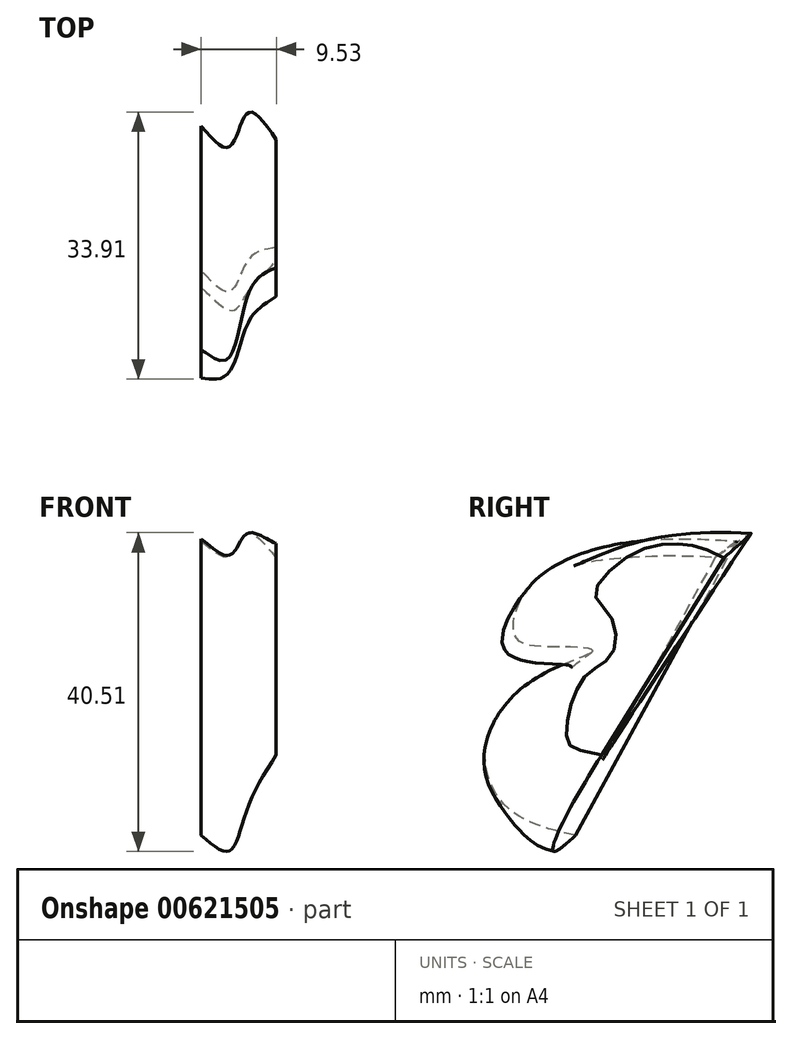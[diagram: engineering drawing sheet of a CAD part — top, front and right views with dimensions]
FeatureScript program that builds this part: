
annotation { "Feature Type Name" : "Feature", "Feature Type Description" : "" }
export const myFeature = defineFeature(function(context is Context, id is Id, definition is map)
    precondition{}
    {
        {
            var Q0;
            Q0=qCreatedBy(makeId("Right.planeOp"),FACE);
            cPlane(context, id + "F0", {"entities" : qUnion([Q0]), "cplaneType" : CPlaneType.OFFSET, "offset" : 3.17 * mm, "width" : 152.4 * mm, "height" : 152.4 * mm});
        }
        {
            var Q0;
            Q0=qCreatedBy(id+"F0.planeOp",FACE);
            cPlane(context, id + "F1", {"entities" : qUnion([Q0]), "cplaneType" : CPlaneType.OFFSET, "offset" : 3.17 * mm, "width" : 152.4 * mm, "height" : 152.4 * mm});
        }
        {
            var Q0;
            Q0=qCreatedBy(id+"F1.planeOp",FACE);
            cPlane(context, id + "F2", {"entities" : qUnion([Q0]), "cplaneType" : CPlaneType.OFFSET, "offset" : 3.17 * mm, "width" : 152.4 * mm, "height" : 152.4 * mm});
        }
        {
            var Q0;
            Q0=qCreatedBy(makeId("Right.planeOp"),FACE);
            var sketch = newSketch(context, id + "F3", { "sketchPlane" : qUnion([Q0])});
            skFitSpline(sketch, "E0", {"points": [v(0, -7.53) * mm, v(-8.5, -4.13) * mm, v(-11.42, 3.64) * mm, v(-4.62, 12.71) * mm, v(2.19, 15.95) * mm, v(-2.35, 16.44) * mm, v(-7.53, 17.57) * mm, v(-5.75, 24.21) * mm, v(6.88, 29.72) * mm, v(20.49, 29.88) * mm], "startDerivative": vector(-82.86, 19.05) * mm, "endDerivative": vector(95.34, -5.58) * mm});
            skLineSegment(sketch, "E1", {"start": v(20.49, 29.88) * mm, "end": v(0, -7.53) * mm});
            skSolve(sketch);
        }
        {
            var Q0;
            Q0=qCreatedBy(id+"F0.planeOp",FACE);
            var sketch = newSketch(context, id + "F4", { "sketchPlane" : qUnion([Q0])});
            skFitSpline(sketch, "E2", {"points": [v(-2.7, -9.56) * mm, v(-8.67, -4.62) * mm, v(-11.1, 2.83) * mm, v(-4.94, 11.1) * mm, v(-0.52, 13.92) * mm, v(-5.05, 14.4) * mm, v(-9.15, 16.6) * mm, v(-4.62, 24.54) * mm, v(5.91, 27.78) * mm, v(17.78, 27.85) * mm], "startDerivative": vector(-82.86, 19.05) * mm, "endDerivative": vector(95.34, -5.58) * mm});
            skLineSegment(sketch, "E3", {"start": v(17.78, 27.85) * mm, "end": v(-2.7, -9.56) * mm});
            skSolve(sketch);
        }
        {
            var Q0;
            Q0=qCreatedBy(id+"F1.planeOp",FACE);
            var sketch = newSketch(context, id + "F5", { "sketchPlane" : qUnion([Q0])});
            skFitSpline(sketch, "E4", {"points": [v(0, -2.83) * mm, v(-3.64, 2.67) * mm, v(-3.48, 7.53) * mm, v(0, 13.2) * mm, v(3.98, 16.89) * mm, v(1.7, 19.2) * mm, v(0, 21.14) * mm, v(3.64, 27.61) * mm, v(12.07, 30.53) * mm, v(22.28, 30.82) * mm], "startDerivative": vector(-82.86, 19.05) * mm, "endDerivative": vector(95.34, -5.58) * mm});
            skLineSegment(sketch, "E5", {"start": v(22.28, 30.82) * mm, "end": v(0, -2.83) * mm});
            skSolve(sketch);
        }
        {
            var Q0;
            Q0=qCreatedBy(id+"F2.planeOp",FACE);
            var sketch = newSketch(context, id + "F6", { "sketchPlane" : qUnion([Q0])});
            skFitSpline(sketch, "E6", {"points": [v(3.32, 2.67) * mm, v(-1, 4.42) * mm, v(-0.6, 9.07) * mm, v(1.71, 13.14) * mm, v(4.65, 15.56) * mm, v(4.46, 20.35) * mm, v(2.48, 23.18) * mm, v(7.47, 28.38) * mm, v(13.55, 29.48) * mm, v(18.82, 27.72) * mm], "startDerivative": vector(-82.86, 19.05) * mm, "endDerivative": vector(52.21, -30.77) * mm});
            skLineSegment(sketch, "E7", {"start": v(18.82, 27.72) * mm, "end": v(3.32, 2.67) * mm});
            skSolve(sketch);
        }
        {
            var Q0;
            Q0=makeQuery(id+"F3.imprint","IMPRINT",FACE,{"disambiguationData":[TD([[makeQuery(id+"F3.imprint","IMPRINT",EDGE,{"derivedFrom":sQuery(id+"F3.wireOp",EDGE,"E0")}),-1.0]])]});
            var Q1;
            Q1=makeQuery(id+"F4.imprint","IMPRINT",FACE,{"disambiguationData":[TD([[makeQuery(id+"F4.imprint","IMPRINT",EDGE,{"derivedFrom":sQuery(id+"F4.wireOp",EDGE,"E2")}),-1.0]])]});
            var Q2;
            Q2=makeQuery(id+"F5.imprint","IMPRINT",FACE,{"disambiguationData":[TD([[makeQuery(id+"F5.imprint","IMPRINT",EDGE,{"derivedFrom":sQuery(id+"F5.wireOp",EDGE,"E4")}),-1.0]])]});
            var Q3;
            Q3=makeQuery(id+"F6.imprint","IMPRINT",FACE,{"disambiguationData":[TD([[makeQuery(id+"F6.imprint","IMPRINT",EDGE,{"derivedFrom":sQuery(id+"F6.wireOp",EDGE,"E6")}),-1.0]])]});
            loft(context, id + "F7", {"sheetProfilesArray" : [{ "sheetProfileEntities" : qUnion([Q0]) }, { "sheetProfileEntities" : qUnion([Q1]) }, { "sheetProfileEntities" : qUnion([Q2]) }, { "sheetProfileEntities" : qUnion([Q3]) }]});
        }
    });
